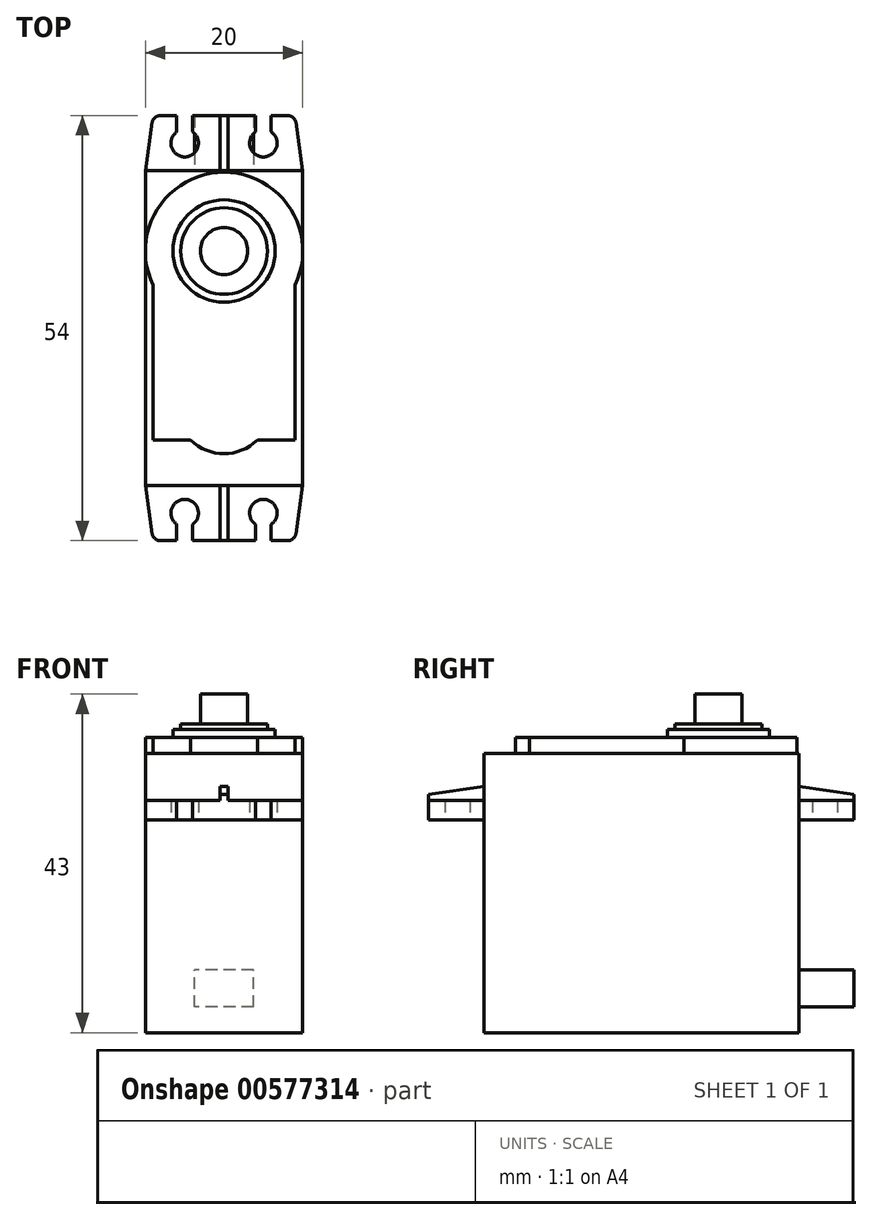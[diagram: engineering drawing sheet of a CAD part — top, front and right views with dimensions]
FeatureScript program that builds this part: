
annotation { "Feature Type Name" : "Feature", "Feature Type Description" : "" }
export const myFeature = defineFeature(function(context is Context, id is Id, definition is map)
    precondition{}
    {
        {
            var Q0;
            Q0=qCreatedBy(makeId("Top.planeOp"),FACE);
            var sketch = newSketch(context, id + "F0", { "sketchPlane" : qUnion([Q0])});
            skLineSegment(sketch, "E0.bottom", {"start": v(0, 0) * mm, "end": v(20, 0) * mm});
            skLineSegment(sketch, "E0.top", {"start": v(0, 40) * mm, "end": v(20, 40) * mm});
            skLineSegment(sketch, "E0.left", {"start": v(0, 0) * mm, "end": v(0, 40) * mm});
            skLineSegment(sketch, "E0.right", {"start": v(20, 0) * mm, "end": v(20, 40) * mm});
            skSolve(sketch);
        }
        {
            var Q0;
            Q0 = qSketchRegion(id + "F0", true);
            extrude(context, id + "F1", {"entities" : qUnion([Q0]), "depth" : 35.5 * mm, "offsetDistance" : 25 * mm});
        }
        {
            var Q0;
            Q0=qCreatedBy(makeId("Top.planeOp"),FACE);
            cPlane(context, id + "F2", {"entities" : qUnion([Q0]), "cplaneType" : CPlaneType.OFFSET, "offset" : 27 * mm, "width" : 150 * mm, "height" : 150 * mm});
        }
        {
            var Q0;
            Q0=qCreatedBy(id+"F2.planeOp",FACE);
            var sketch = newSketch(context, id + "F3", { "sketchPlane" : qUnion([Q0])});
            skLineSegment(sketch, "E1.0.0", {"start": v(20, 40) * mm, "end": v(0, 40) * mm});
            skLineSegment(sketch, "E1.0.1", {"start": v(0, 40) * mm, "end": v(0, 0) * mm});
            skLineSegment(sketch, "E1.0.2", {"start": v(0, 0) * mm, "end": v(20, 0) * mm});
            skLineSegment(sketch, "E1.0.3", {"start": v(20, 0) * mm, "end": v(20, 40) * mm});
            skLineSegment(sketch, "E2", {"start": v(0, 40) * mm, "end": v(0.88, 46.14) * mm});
            skLineSegment(sketch, "E3", {"start": v(1.87, 47) * mm, "end": v(4, 47) * mm});
            skLineSegment(sketch, "E4", {"start": v(19.12, 46.14) * mm, "end": v(20, 40) * mm});
            skLineSegment(sketch, "E5", {"start": v(20, 0) * mm, "end": v(19.12, -6.14) * mm});
            skLineSegment(sketch, "E6", {"start": v(18.13, -7) * mm, "end": v(16, -7) * mm});
            skLineSegment(sketch, "E7", {"start": v(0.88, -6.14) * mm, "end": v(0, 0) * mm});
            skPoint(sketch, "E8.visualSharp", {"position": v(1, 47) * mm});
            skArc(sketch, "E8.filletArc", {"start": v(1.87, 47) * mm, "mid": v(1.21, 46.76) * mm, "end": v(0.88, 46.14) * mm});
            skPoint(sketch, "E9.visualSharp", {"position": v(19, 47) * mm});
            skArc(sketch, "E9.filletArc", {"start": v(19.12, 46.14) * mm, "mid": v(18.79, 46.76) * mm, "end": v(18.13, 47) * mm});
            skArc(sketch, "E10", {"start": v(4, 44.94) * mm, "mid": v(5, 41.75) * mm, "end": v(6, 44.94) * mm});
            skArc(sketch, "E11", {"start": v(14, 44.94) * mm, "mid": v(15, 41.75) * mm, "end": v(16, 44.94) * mm});
            skArc(sketch, "E12", {"start": v(6, -4.94) * mm, "mid": v(5, -1.75) * mm, "end": v(4, -4.94) * mm});
            skArc(sketch, "E13", {"start": v(16, -4.94) * mm, "mid": v(15, -1.75) * mm, "end": v(14, -4.94) * mm});
            skPoint(sketch, "E14.visualSharp", {"position": v(1, -7) * mm});
            skArc(sketch, "E14.filletArc", {"start": v(0.88, -6.14) * mm, "mid": v(1.21, -6.76) * mm, "end": v(1.87, -7) * mm});
            skPoint(sketch, "E15.visualSharp", {"position": v(19, -7) * mm});
            skArc(sketch, "E15.filletArc", {"start": v(18.13, -7) * mm, "mid": v(18.79, -6.76) * mm, "end": v(19.12, -6.14) * mm});
            skLineSegment(sketch, "E16", {"start": v(4, 44.94) * mm, "end": v(4, 47) * mm});
            skLineSegment(sketch, "E17", {"start": v(6, 44.94) * mm, "end": v(6, 47) * mm});
            skLineSegment(sketch, "E18.1.0.0", {"start": v(16, 44.94) * mm, "end": v(16, 47) * mm});
            skLineSegment(sketch, "E18.1.0.1", {"start": v(14, 44.94) * mm, "end": v(14, 47) * mm});
            skLineSegment(sketch, "E18.direction1", {"start": v(6, 44.94) * mm, "end": v(16, 44.94) * mm, "construction": true});
            skLineSegment(sketch, "E19.trimOffspring", {"start": v(6, 47) * mm, "end": v(14, 47) * mm});
            skLineSegment(sketch, "E20.trimOffspring", {"start": v(16, 47) * mm, "end": v(18.13, 47) * mm});
            skLineSegment(sketch, "E21", {"start": v(4, -4.94) * mm, "end": v(4, -7) * mm});
            skLineSegment(sketch, "E22", {"start": v(6, -4.94) * mm, "end": v(6, -7) * mm});
            skLineSegment(sketch, "E23.trimOffspring", {"start": v(4, -7) * mm, "end": v(1.87, -7) * mm});
            skLineSegment(sketch, "E24.1.0.0", {"start": v(16, -4.94) * mm, "end": v(16, -7) * mm});
            skLineSegment(sketch, "E24.1.0.1", {"start": v(14, -4.94) * mm, "end": v(14, -7) * mm});
            skLineSegment(sketch, "E24.direction1", {"start": v(6, -7) * mm, "end": v(14, -7) * mm, "construction": true});
            skLineSegment(sketch, "E25.trimOffspring", {"start": v(14, -7) * mm, "end": v(6, -7) * mm});
            skSolve(sketch);
        }
        {
            var Q0;
            Q0 = qSketchRegion(id + "F3", true);
            extrude(context, id + "F4", {"entities" : qUnion([Q0]), "operationType" : NewBodyOperationType.ADD, "depth" : 2.5 * mm, "offsetDistance" : 25 * mm});
        }
        {
            var Q0;
            Q0=qCreatedBy(makeId("Right.planeOp"),FACE);
            cPlane(context, id + "F5", {"entities" : qUnion([Q0]), "cplaneType" : CPlaneType.OFFSET, "offset" : 10 * mm, "width" : 150 * mm, "height" : 150 * mm});
        }
        {
            var Q0;
            Q0=qCreatedBy(id+"F5.planeOp",FACE);
            var sketch = newSketch(context, id + "F6", { "sketchPlane" : qUnion([Q0])});
            skPoint(sketch, "E26.0", {"position": v(40, 29.5) * mm});
            skPoint(sketch, "E27.0", {"position": v(0, 29.5) * mm});
            skLineSegment(sketch, "E28", {"start": v(40, 29.5) * mm, "end": v(40, 31.25) * mm});
            skLineSegment(sketch, "E29", {"start": v(0, 29.5) * mm, "end": v(0, 31.25) * mm});
            skLineSegment(sketch, "E30", {"start": v(40, 29.5) * mm, "end": v(47, 29.5) * mm});
            skLineSegment(sketch, "E31", {"start": v(47, 29.5) * mm, "end": v(47, 30.25) * mm});
            skLineSegment(sketch, "E32", {"start": v(47, 30.25) * mm, "end": v(40, 31.25) * mm});
            skLineSegment(sketch, "E33", {"start": v(0, 29.5) * mm, "end": v(-7, 29.5) * mm});
            skLineSegment(sketch, "E34", {"start": v(-7, 29.5) * mm, "end": v(-7, 30.25) * mm});
            skLineSegment(sketch, "E35", {"start": v(-7, 30.25) * mm, "end": v(0, 31.25) * mm});
            skSolve(sketch);
        }
        {
            var Q0;
            Q0 = qSketchRegion(id + "F6", true);
            extrude(context, id + "F7", {"entities" : qUnion([Q0]), "operationType" : NewBodyOperationType.ADD, "endBound" : BoundingType.SYMMETRIC, "depth" : 1 * mm, "offsetDistance" : 25 * mm});
        }
        {
            var Q0;
            Q0=makeQuery(id+"F1.opExtrude","CAP_FACE",FACE,{"disambiguationData":[OSD([sQuery(id+"F0.wireOp",EDGE,"E0.bottom"),sQuery(id+"F0.wireOp",EDGE,"E0.top"),sQuery(id+"F0.wireOp",EDGE,"E0.left"),sQuery(id+"F0.wireOp",EDGE,"E0.right")])],"isStart":false});
            var sketch = newSketch(context, id + "F8", { "sketchPlane" : qUnion([Q0])});
            skArc(sketch, "E36", {"start": v(19, 25.44) * mm, "mid": v(10, 39.8) * mm, "end": v(1, 25.44) * mm});
            skPoint(sketch, "E36.centerSnap0", {"position": v(10, 0) * mm});
            skLineSegment(sketch, "E37", {"start": v(10, 39.8) * mm, "end": v(10, 5.8) * mm, "construction": true});
            skPoint(sketch, "E37.startSnap0", {"position": v(10, 40) * mm});
            skPoint(sketch, "E37.endSnap0", {"position": v(10, 40) * mm});
            skLineSegment(sketch, "E38.bottom", {"start": v(19, 5.8) * mm, "end": v(14.24, 5.8) * mm});
            skLineSegment(sketch, "E38.left", {"start": v(19, 5.8) * mm, "end": v(19, 25.44) * mm});
            skLineSegment(sketch, "E38.right", {"start": v(1, 5.8) * mm, "end": v(1, 25.44) * mm});
            skPoint(sketch, "E39.orphan", {"position": v(1, 39.8) * mm});
            skArc(sketch, "E40", {"start": v(5.76, 5.8) * mm, "mid": v(10, 4.05) * mm, "end": v(14.24, 5.8) * mm});
            skLineSegment(sketch, "E41.trimOffspring", {"start": v(5.76, 5.8) * mm, "end": v(1, 5.8) * mm});
            skSolve(sketch);
        }
        {
            var Q0;
            Q0 = qSketchRegion(id + "F8", true);
            extrude(context, id + "F9", {"entities" : qUnion([Q0]), "operationType" : NewBodyOperationType.ADD, "depth" : 2 * mm, "offsetDistance" : 25 * mm});
        }
        {
            var Q0;
            Q0=makeQuery(id+"F9.opExtrude","CAP_FACE",FACE,{"disambiguationData":[OSD([sQuery(id+"F8.wireOp",EDGE,"E36"),sQuery(id+"F8.wireOp",EDGE,"E38.bottom"),sQuery(id+"F8.wireOp",EDGE,"E38.left"),sQuery(id+"F8.wireOp",EDGE,"E38.right"),sQuery(id+"F8.wireOp",EDGE,"E40"),sQuery(id+"F8.wireOp",EDGE,"E41.trimOffspring")])],"isStart":false});
            var sketch = newSketch(context, id + "F10", { "sketchPlane" : qUnion([Q0])});
            skCircle(sketch, "E42", {"center": v(10, 29.8) * mm, "radius": 6.5 * mm});
            skSolve(sketch);
        }
        {
            var Q0;
            Q0 = qSketchRegion(id + "F10", true);
            extrude(context, id + "F11", {"entities" : qUnion([Q0]), "operationType" : NewBodyOperationType.ADD, "depth" : 1 * mm, "offsetDistance" : 25 * mm});
        }
        {
            var Q0;
            Q0=makeQuery(id+"F11.opExtrude","CAP_FACE",FACE,{"disambiguationData":[OSD([sQuery(id+"F10.wireOp",EDGE,"E42")])],"isStart":false});
            var sketch = newSketch(context, id + "F12", { "sketchPlane" : qUnion([Q0])});
            skCircle(sketch, "E43", {"center": v(10, 29.8) * mm, "radius": 5.5 * mm});
            skSolve(sketch);
        }
        {
            var Q0;
            Q0 = qSketchRegion(id + "F12", true);
            extrude(context, id + "F13", {"entities" : qUnion([Q0]), "operationType" : NewBodyOperationType.ADD, "depth" : .75 * mm, "offsetDistance" : 25 * mm});
        }
        {
            var Q0;
            Q0=makeQuery(id+"F13.opExtrude","CAP_FACE",FACE,{"disambiguationData":[OSD([sQuery(id+"F12.wireOp",EDGE,"E43")])],"isStart":false});
            var sketch = newSketch(context, id + "F14", { "sketchPlane" : qUnion([Q0])});
            skCircle(sketch, "E44", {"center": v(10, 29.8) * mm, "radius": 3 * mm});
            skSolve(sketch);
        }
        {
            var Q0;
            Q0 = qSketchRegion(id + "F14", true);
            extrude(context, id + "F15", {"entities" : qUnion([Q0]), "depth" : 3.75 * mm, "offsetDistance" : 25 * mm});
        }
        {
            var Q0;
            {var subQ2=sQuery(id+"F0.wireOp",EDGE,"E0.right");var subQ3=sQuery(id+"F0.wireOp",EDGE,"E0.left");var subQ4=sQuery(id+"F0.wireOp",EDGE,"E0.top");Q0=makeQuery(id+"F4.boolean.opBoolean","SPLIT",FACE,{"disambiguationData":[TD([makeQuery(id+"F1.opExtrude","CAP_FACE",FACE,{"disambiguationData":[OSD([sQuery(id+"F0.wireOp",EDGE,"E0.bottom"),subQ4,subQ3,subQ2])],"isStart":true})])],"derivedFrom":makeQuery(id+"F1.opExtrude","SWEPT_FACE",FACE,{"disambiguationData":[OSD([subQ4])]})});}
            var sketch = newSketch(context, id + "F16", { "sketchPlane" : qUnion([Q0])});
            skLineSegment(sketch, "E45.bottom", {"start": v(-13.75, 3.25) * mm, "end": v(-6.25, 3.25) * mm});
            skLineSegment(sketch, "E45.top", {"start": v(-13.75, 8) * mm, "end": v(-6.25, 8) * mm});
            skLineSegment(sketch, "E45.left", {"start": v(-13.75, 3.25) * mm, "end": v(-13.75, 8) * mm});
            skLineSegment(sketch, "E45.right", {"start": v(-6.25, 3.25) * mm, "end": v(-6.25, 8) * mm});
            skSolve(sketch);
        }
        {
            var Q0;
            Q0 = qSketchRegion(id + "F16", true);
            extrude(context, id + "F17", {"entities" : qUnion([Q0]), "operationType" : NewBodyOperationType.ADD, "depth" : 7 * mm, "offsetDistance" : 25 * mm});
        }
    });
